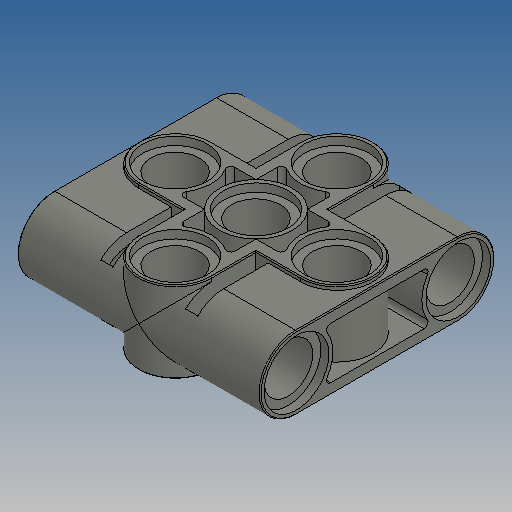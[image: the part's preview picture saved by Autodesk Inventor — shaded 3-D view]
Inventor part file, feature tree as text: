
AUTODESK INVENTOR PART (.ipt)
format: ipt  version: 2025 (Build 290162010, 162A)  size: 481,792 bytes
history: native  units: in
note: dims shown in document units (in); Inventor stores cm internally (conversion verified against a paired STEP export)
features: extrude x8, sketch x3, mirror x1, fillet x1
ambient origin geometry x8: Origin, YZ Plane, XZ Plane, XY Plane, X Axis, Y Axis, Z Axis, Center Point
bodies: Solid1 (feature_tree)
feature tree (13):
  extrude  "Extrusion1"  Depth=0.2835in
  sketch  "Sketch3"  dims[d4=45.0deg d5=0.9449in]
  extrude  "Extrusion3"  Depth=0.9449in
  extrude  "Extrusion2"  Depth=0.2835in
  extrude  "Extrusion4"  Depth=0.189in
  extrude  "Extrusion5"  Depth=0.252in
  extrude  "Extrusion8"  Depth=0.315in
  sketch  "Sketch4"  dims[d6=0.0in d7=0.2835in d8=0.189in d9=0.252in d10=0.315in d11=0.0in d12=0.315in d13=0.0in d14=0.0472in d15=0.1002in d16=0.315in d17=0.0in d18=0.252in d19=0.0in d20=0.189in d21=0.252in d22=0.315in d23=0.0in d24=0.0315in d25=0.0in d26=0.063in d27=0.0in d28=0.0039in d29=0.0157in]
  extrude  "Extrusion6"  TaperAngle=0.0deg  [1 undecoded]
  extrude  "Extrusion7"  Depth=0.315in TaperAngle=0.0deg
  mirror  "Mirror1"
  fillet  "Fillet1"  Radius=0.0472in
  sketch  "Sketch2"  dims[d2=0.6299in d3=0.2835in]
note: 1 required parameter value undecoded (feature->parameter linkage not recoverable at this tier; creation-order binding heuristic only, values carry confidence <= 0.55)
